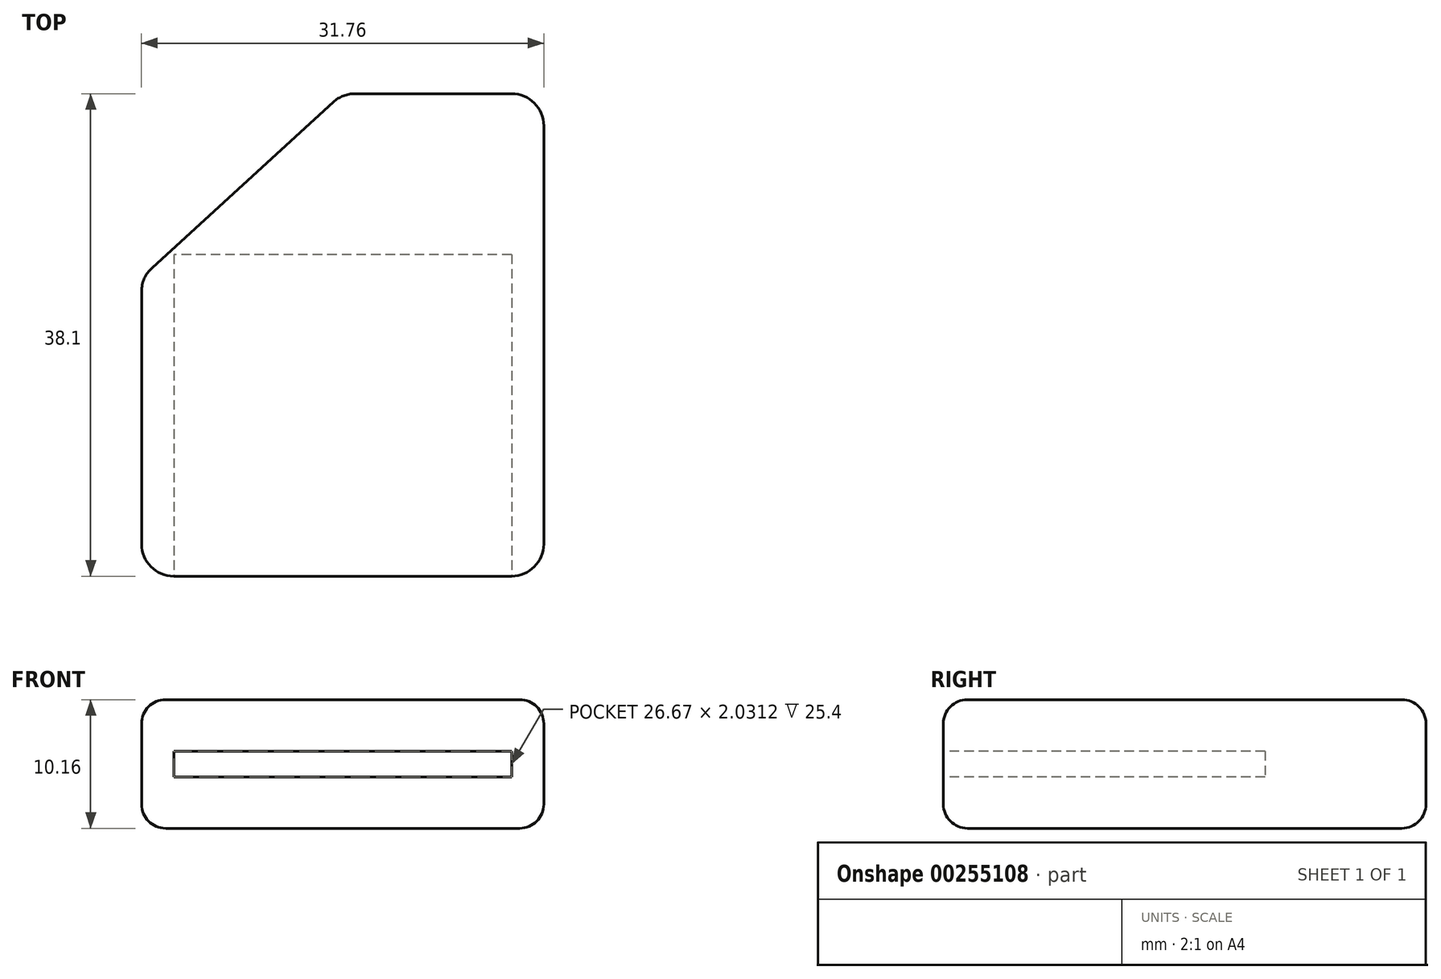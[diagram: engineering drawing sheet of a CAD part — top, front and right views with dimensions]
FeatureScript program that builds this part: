
annotation { "Feature Type Name" : "Feature", "Feature Type Description" : "" }
export const myFeature = defineFeature(function(context is Context, id is Id, definition is map)
    precondition{}
    {
        {
            var Q0;
            Q0=qCreatedBy(makeId("Top.planeOp"),FACE);
            var sketch = newSketch(context, id + "F0", { "sketchPlane" : qUnion([Q0])});
            skLineSegment(sketch, "E0.bottom", {"start": v(15.88, -19.05) * mm, "end": v(-15.88, -19.05) * mm});
            skLineSegment(sketch, "E0.top", {"start": v(15.87, 19.05) * mm, "end": v(0, 19.05) * mm});
            skLineSegment(sketch, "E0.left", {"start": v(15.88, -19.05) * mm, "end": v(15.88, 19.05) * mm});
            skLineSegment(sketch, "E0.right", {"start": v(-15.88, -19.05) * mm, "end": v(-15.88, 4.54) * mm});
            skPoint(sketch, "E0.middle", {"position": v(0, 0) * mm});
            skLineSegment(sketch, "E1", {"start": v(0, 19.05) * mm, "end": v(-15.88, 4.54) * mm});
            skPoint(sketch, "E2", {"position": v(0, 19.05) * mm});
            skPoint(sketch, "E3.orphan", {"position": v(-15.87, 19.05) * mm});
            skSolve(sketch);
        }
        {
            var Q0;
            Q0 = qSketchRegion(id + "F0", true);
            extrude(context, id + "F1", {"entities" : qUnion([Q0]), "depth" : 5.08 * mm, "hasSecondDirection" : true, "secondDirectionOppositeDirection" : true, "secondDirectionDepth" : 5.08 * mm});
        }
        {
            var Q0;
            Q0=makeQuery(id+"F1.opExtrude","CAP_FACE",FACE,{"disambiguationData":[OSD([sQuery(id+"F0.wireOp",EDGE,"E0.bottom"),sQuery(id+"F0.wireOp",EDGE,"E0.top"),sQuery(id+"F0.wireOp",EDGE,"E0.left"),sQuery(id+"F0.wireOp",EDGE,"E0.right"),sQuery(id+"F0.wireOp",EDGE,"E1")])],"isStart":false});
            var Q1;
            Q1=makeQuery(id+"F1.opExtrude","CAP_FACE",FACE,{"disambiguationData":[OSD([sQuery(id+"F0.wireOp",EDGE,"E0.bottom"),sQuery(id+"F0.wireOp",EDGE,"E0.top"),sQuery(id+"F0.wireOp",EDGE,"E0.left"),sQuery(id+"F0.wireOp",EDGE,"E0.right"),sQuery(id+"F0.wireOp",EDGE,"E1")])],"isStart":true});
            fillet(context, id + "F2", {"entities" : qUnion([Q0, Q1]), "radius" : 1.9 * mm, "tangentPropagation" : true, "allowEdgeOverflow" : false});
        }
        {
            var Q0;
            Q0=makeQuery(id+"F1.opExtrude","SWEPT_FACE",FACE,{"disambiguationData":[OSD([sQuery(id+"F0.wireOp",EDGE,"E0.bottom")])]});
            var Q1;
            Q1=makeQuery(id+"F1.opExtrude","SWEPT_FACE",FACE,{"disambiguationData":[OSD([sQuery(id+"F0.wireOp",EDGE,"E0.right")])]});
            var Q2;
            Q2=makeQuery(id+"F1.opExtrude","SWEPT_FACE",FACE,{"disambiguationData":[OSD([sQuery(id+"F0.wireOp",EDGE,"E1")])]});
            var Q3;
            Q3=makeQuery(id+"F1.opExtrude","SWEPT_FACE",FACE,{"disambiguationData":[OSD([sQuery(id+"F0.wireOp",EDGE,"E0.top")])]});
            var Q4;
            Q4=makeQuery(id+"F1.opExtrude","SWEPT_FACE",FACE,{"disambiguationData":[OSD([sQuery(id+"F0.wireOp",EDGE,"E0.left")])]});
            fillet(context, id + "F3", {"entities" : qUnion([Q0, Q1, Q2, Q3, Q4]), "radius" : 2.54 * mm, "tangentPropagation" : true, "allowEdgeOverflow" : false});
        }
        {
            var Q0;
            Q0=makeQuery(id+"F1.opExtrude","SWEPT_FACE",FACE,{"disambiguationData":[OSD([sQuery(id+"F0.wireOp",EDGE,"E0.bottom")])]});
            var sketch = newSketch(context, id + "F4", { "sketchPlane" : qUnion([Q0])});
            skLineSegment(sketch, "E4.bottom", {"start": v(13.33, -1.02) * mm, "end": v(-13.33, -1.02) * mm});
            skLineSegment(sketch, "E4.top", {"start": v(13.33, 1.02) * mm, "end": v(-13.33, 1.02) * mm});
            skLineSegment(sketch, "E4.left", {"start": v(13.33, -1.02) * mm, "end": v(13.33, 1.02) * mm});
            skLineSegment(sketch, "E4.right", {"start": v(-13.33, -1.02) * mm, "end": v(-13.33, 1.02) * mm});
            skPoint(sketch, "E4.middle", {"position": v(0, 0) * mm});
            skSolve(sketch);
        }
        {
            var Q0;
            Q0 = qSketchRegion(id + "F4", true);
            extrude(context, id + "F5", {"entities" : qUnion([Q0]), "operationType" : NewBodyOperationType.REMOVE, "oppositeDirection" : true, "depth" : 25.4 * mm});
        }
    });
